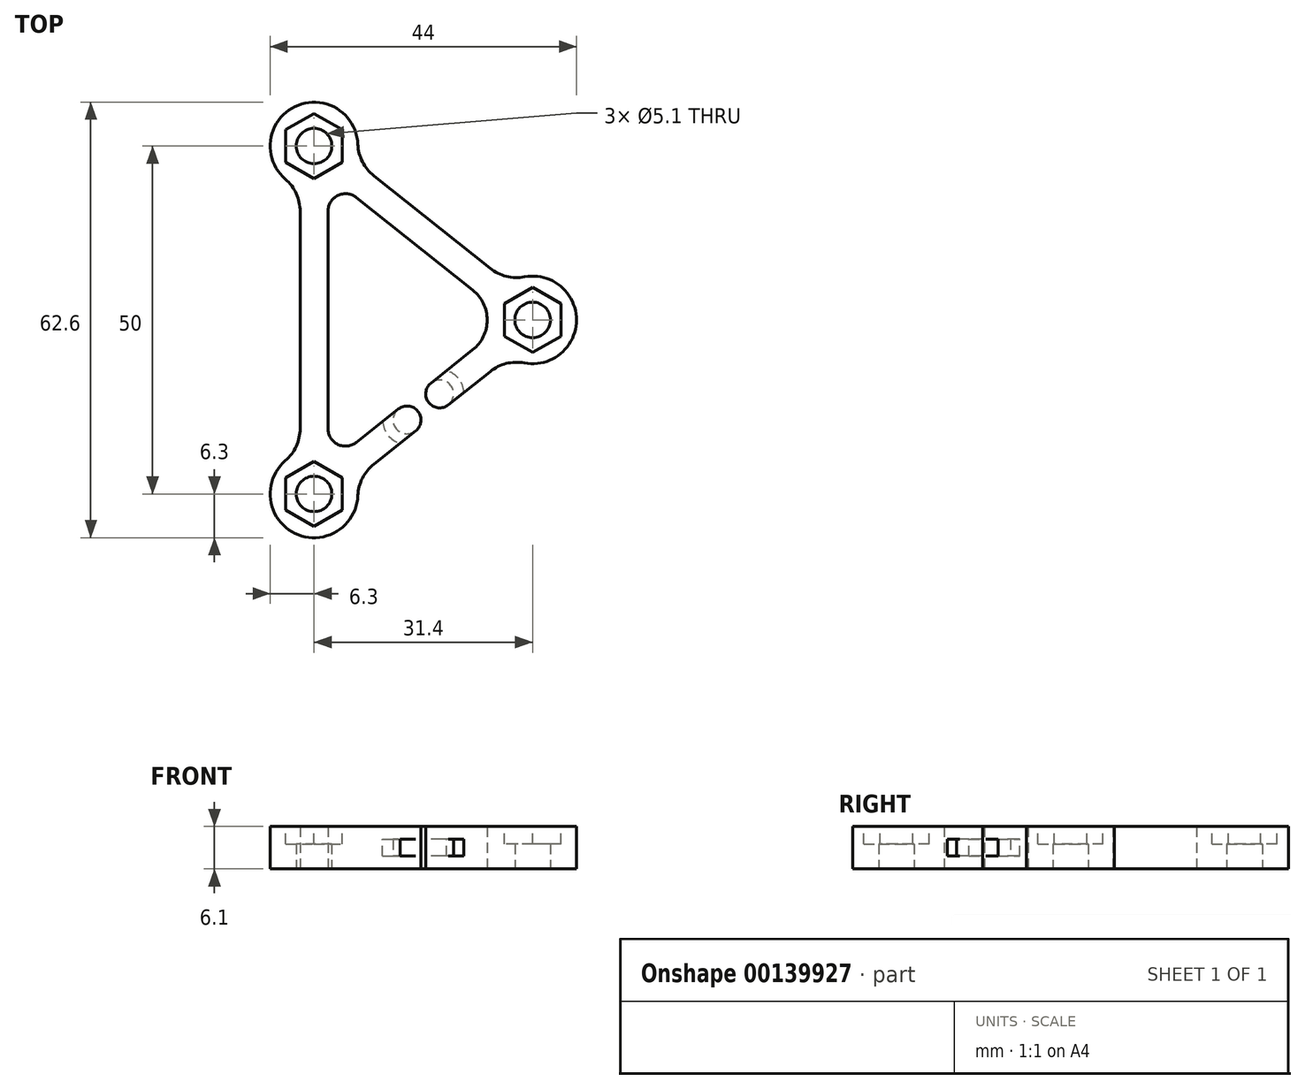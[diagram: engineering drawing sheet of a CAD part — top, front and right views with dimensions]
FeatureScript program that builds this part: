
annotation { "Feature Type Name" : "Feature", "Feature Type Description" : "" }
export const myFeature = defineFeature(function(context is Context, id is Id, definition is map)
    precondition{}
    {
        {
            var Q0;
            Q0=qCreatedBy(makeId("Top.planeOp"),FACE);
            var sketch = newSketch(context, id + "F0", { "sketchPlane" : qUnion([Q0])});
            skCircle(sketch, "E0", {"center": v(-31.4, 25) * mm, "radius": 2.55 * mm});
            skCircle(sketch, "E1", {"center": v(-31.4, -25) * mm, "radius": 2.55 * mm});
            skCircle(sketch, "E2", {"center": v(0, 0) * mm, "radius": 2.55 * mm});
            skArc(sketch, "E3", {"start": v(-25.1, 25.25) * mm, "mid": v(-34.14, 30.68) * mm, "end": v(-35.52, 20.23) * mm});
            skArc(sketch, "E4", {"start": v(-35.52, -20.23) * mm, "mid": v(-34.14, -30.68) * mm, "end": v(-25.1, -25.25) * mm});
            skArc(sketch, "E5", {"start": v(-1.17, -6.2) * mm, "mid": v(6.3, 0) * mm, "end": v(-1.17, 6.2) * mm});
            skLineSegment(sketch, "E6", {"start": v(-25.3, 17.59) * mm, "end": v(-8.6, 4.28) * mm});
            skLineSegment(sketch, "E7", {"start": v(-22.8, 20.72) * mm, "end": v(-6.1, 7.41) * mm});
            skLineSegment(sketch, "E8", {"start": v(-31.4, 25) * mm, "end": v(0, 0) * mm, "construction": true});
            skLineSegment(sketch, "E9", {"start": v(0, 0) * mm, "end": v(-31.4, -25) * mm, "construction": true});
            skLineSegment(sketch, "E10", {"start": v(-31.4, -25) * mm, "end": v(-31.4, 25) * mm, "construction": true});
            skArc(sketch, "E11", {"start": v(-25.3, 17.59) * mm, "mid": v(-27.97, 17.89) * mm, "end": v(-29.4, 15.61) * mm});
            skArc(sketch, "E12", {"start": v(-29.4, -15.61) * mm, "mid": v(-27.97, -17.89) * mm, "end": v(-25.3, -17.59) * mm});
            skArc(sketch, "E13", {"start": v(-8.6, -4.28) * mm, "mid": v(-6.53, 0) * mm, "end": v(-8.6, 4.28) * mm});
            skArc(sketch, "E14", {"start": v(-35.52, -20.23) * mm, "mid": v(-33.95, -18.15) * mm, "end": v(-33.4, -15.61) * mm});
            skArc(sketch, "E15", {"start": v(-22.8, -20.72) * mm, "mid": v(-24.45, -22.73) * mm, "end": v(-25.1, -25.25) * mm});
            skArc(sketch, "E16", {"start": v(-33.4, 15.61) * mm, "mid": v(-33.95, 18.15) * mm, "end": v(-35.52, 20.23) * mm});
            skArc(sketch, "E17", {"start": v(-25.1, 25.25) * mm, "mid": v(-24.45, 22.73) * mm, "end": v(-22.8, 20.72) * mm});
            skArc(sketch, "E18", {"start": v(-6.1, 7.41) * mm, "mid": v(-3.77, 6.26) * mm, "end": v(-1.17, 6.2) * mm});
            skArc(sketch, "E19", {"start": v(-1.17, -6.2) * mm, "mid": v(-3.77, -6.26) * mm, "end": v(-6.1, -7.41) * mm});
            skLineSegment(sketch, "E20", {"start": v(-25.3, 17.59) * mm, "end": v(-22.8, 20.72) * mm, "construction": true});
            skLineSegment(sketch, "E21", {"start": v(-8.6, 4.28) * mm, "end": v(-6.1, 7.41) * mm, "construction": true});
            skLineSegment(sketch, "E22", {"start": v(-8.6, -4.28) * mm, "end": v(-6.1, -7.41) * mm, "construction": true});
            skLineSegment(sketch, "E23", {"start": v(-33.4, -15.61) * mm, "end": v(-29.4, -15.61) * mm, "construction": true});
            skLineSegment(sketch, "E24", {"start": v(-22.8, -20.72) * mm, "end": v(-25.3, -17.59) * mm, "construction": true});
            skLineSegment(sketch, "E25", {"start": v(-33.4, -15.61) * mm, "end": v(-33.4, 15.61) * mm});
            skLineSegment(sketch, "E26", {"start": v(-29.4, -15.61) * mm, "end": v(-29.4, 15.61) * mm});
            skLineSegment(sketch, "E27", {"start": v(-33.4, 15.61) * mm, "end": v(-29.4, 15.61) * mm, "construction": true});
            skLineSegment(sketch, "E28", {"start": v(-25.3, -17.59) * mm, "end": v(-19.3, -12.8) * mm});
            skLineSegment(sketch, "E29", {"start": v(-14.6, -9.07) * mm, "end": v(-8.6, -4.28) * mm});
            skLineSegment(sketch, "E30", {"start": v(-22.8, -20.72) * mm, "end": v(-16.8, -15.93) * mm});
            skLineSegment(sketch, "E31", {"start": v(-6.1, -7.41) * mm, "end": v(-12.1, -12.2) * mm});
            skArc(sketch, "E32", {"start": v(-16.8, -15.93) * mm, "mid": v(-16.48, -13.12) * mm, "end": v(-19.3, -12.8) * mm});
            skArc(sketch, "E33", {"start": v(-14.6, -9.07) * mm, "mid": v(-14.92, -11.88) * mm, "end": v(-12.1, -12.2) * mm});
            skLineSegment(sketch, "E34", {"start": v(-29.4, 0) * mm, "end": v(0, 0) * mm, "construction": true});
            skSolve(sketch);
        }
        {
            var Q0;
            Q0=makeQuery(id+"F0.imprint","IMPRINT",FACE,{"disambiguationData":[TD([[makeQuery(id+"F0.imprint","IMPRINT",EDGE,{"derivedFrom":sQuery(id+"F0.wireOp",EDGE,"E0")}),-1.0]])]});
            extrude(context, id + "F1", {"entities" : qUnion([Q0]), "depth" : 6.1 * mm});
        }
        {
            var Q0;
            Q0=makeQuery(id+"F1.opExtrude","CAP_FACE",FACE,{"disambiguationData":[OSD([sQuery(id+"F0.wireOp",EDGE,"E0"),sQuery(id+"F0.wireOp",EDGE,"E1"),sQuery(id+"F0.wireOp",EDGE,"E2"),sQuery(id+"F0.wireOp",EDGE,"E3"),sQuery(id+"F0.wireOp",EDGE,"E4"),sQuery(id+"F0.wireOp",EDGE,"E5"),sQuery(id+"F0.wireOp",EDGE,"T5Vw66OG-G5OR-DHDx-KvU7-dnTMRq0o1A0g"),sQuery(id+"F0.wireOp",EDGE,"8mzCXc7P-Lu7A-tcA2-hDls-zUZMRrlwUirj"),sQuery(id+"F0.wireOp",EDGE,"n4Ubmgs8-MzYA-ilAs-um63-DOsCIZ42xYd5"),sQuery(id+"F0.wireOp",EDGE,"iCspHw3C-Pdpp-QPBW-yDHl-MGOv44Ga2VXa"),sQuery(id+"F0.wireOp",EDGE,"xnWTmErK-ZSIG-ryMW-Ekzr-RR3PqCajZfuL"),sQuery(id+"F0.wireOp",EDGE,"AKW5OVUo-PFRE-jSi0-v7oE-Iw4JobIG5vWv"),sQuery(id+"F0.wireOp",EDGE,"E6"),sQuery(id+"F0.wireOp",EDGE,"JkiSf5jC-OJZR-1wmq-AVkU-QwjWYPwXVpW3"),sQuery(id+"F0.wireOp",EDGE,"9YlTFYq7-sXvY-dmJ4-6YRE-gBgDyT6P94yA")])],"isStart":false});
            var sketch = newSketch(context, id + "F2", { "sketchPlane" : qUnion([Q0])});
            skCircle(sketch, "E35.cCircle", {"center": v(-31.4, 25) * mm, "radius": 4.05 * mm, "construction": true});
            skLineSegment(sketch, "E35.0", {"start": v(-27.35, 27.34) * mm, "end": v(-27.35, 22.66) * mm});
            skLineSegment(sketch, "E35.1", {"start": v(-27.35, 22.66) * mm, "end": v(-31.4, 20.32) * mm});
            skLineSegment(sketch, "E35.2", {"start": v(-31.4, 20.32) * mm, "end": v(-35.45, 22.66) * mm});
            skLineSegment(sketch, "E35.3", {"start": v(-35.45, 22.66) * mm, "end": v(-35.45, 27.34) * mm});
            skLineSegment(sketch, "E35.4", {"start": v(-35.45, 27.34) * mm, "end": v(-31.4, 29.68) * mm});
            skLineSegment(sketch, "E35.5", {"start": v(-31.4, 29.68) * mm, "end": v(-27.35, 27.34) * mm});
            skPoint(sketch, "E35.0.midPoint", {"position": v(-27.35, 25) * mm});
            skCircle(sketch, "E36.cCircle", {"center": v(-31.4, -25) * mm, "radius": 4.05 * mm, "construction": true});
            skLineSegment(sketch, "E36.0", {"start": v(-27.35, -22.66) * mm, "end": v(-27.35, -27.34) * mm});
            skLineSegment(sketch, "E36.1", {"start": v(-27.35, -27.34) * mm, "end": v(-31.4, -29.68) * mm});
            skLineSegment(sketch, "E36.2", {"start": v(-31.4, -29.68) * mm, "end": v(-35.45, -27.34) * mm});
            skLineSegment(sketch, "E36.3", {"start": v(-35.45, -27.34) * mm, "end": v(-35.45, -22.66) * mm});
            skLineSegment(sketch, "E36.4", {"start": v(-35.45, -22.66) * mm, "end": v(-31.4, -20.32) * mm});
            skLineSegment(sketch, "E36.5", {"start": v(-31.4, -20.32) * mm, "end": v(-27.35, -22.66) * mm});
            skPoint(sketch, "E36.0.midPoint", {"position": v(-27.35, -25) * mm});
            skCircle(sketch, "E37.cCircle", {"center": v(0, 0) * mm, "radius": 4.05 * mm, "construction": true});
            skLineSegment(sketch, "E37.0", {"start": v(-4.05, -2.34) * mm, "end": v(-4.05, 2.34) * mm});
            skLineSegment(sketch, "E37.1", {"start": v(-4.05, 2.34) * mm, "end": v(0, 4.68) * mm});
            skLineSegment(sketch, "E37.2", {"start": v(0, 4.68) * mm, "end": v(4.05, 2.34) * mm});
            skLineSegment(sketch, "E37.3", {"start": v(4.05, 2.34) * mm, "end": v(4.05, -2.34) * mm});
            skLineSegment(sketch, "E37.4", {"start": v(4.05, -2.34) * mm, "end": v(0, -4.68) * mm});
            skLineSegment(sketch, "E37.5", {"start": v(0, -4.68) * mm, "end": v(-4.05, -2.34) * mm});
            skPoint(sketch, "E37.0.midPoint", {"position": v(-4.05, 0) * mm});
            skSolve(sketch);
        }
        {
            var Q0;
            Q0=qSketchRegion(id+"F2",true);
            extrude(context, id + "F3", {"entities" : qUnion([Q0]), "operationType" : NewBodyOperationType.REMOVE, "oppositeDirection" : true, "depth" : 2.5 * mm});
        }
        {
            var Q0;
            Q0=qCreatedBy(makeId("Top.planeOp"),FACE);
            var Q1;
            Q1=makeQuery(id+"F2.imprint","IMPRINT",FACE,{"disambiguationData":[TD([[makeQuery(id+"F2.imprint","IMPRINT",EDGE,{"derivedFrom":sQuery(id+"F2.wireOp",EDGE,"E35.0")}),1.0]])]});
            cPlane(context, id + "F4", {"entities" : qUnion([Q0, Q1]), "cplaneType" : CPlaneType.MID_PLANE, "offset" : 3 * mm, "oppositeDirection" : true, "width" : 150 * mm, "height" : 150 * mm});
        }
        {
            var Q0;
            Q0=qCreatedBy(id+"F4.planeOp",FACE);
            var sketch = newSketch(context, id + "F5", { "sketchPlane" : qUnion([Q0])});
            skLineSegment(sketch, "E38", {"start": v(-16.8, -15.93) * mm, "end": v(-16.8, -15.93) * mm});
            skLineSegment(sketch, "E39", {"start": v(-19.3, -12.8) * mm, "end": v(-19.3, -12.8) * mm});
            skLineSegment(sketch, "E40", {"start": v(-12.1, -12.2) * mm, "end": v(-12.1, -12.2) * mm});
            skLineSegment(sketch, "E41", {"start": v(-14.6, -9.07) * mm, "end": v(-14.6, -9.07) * mm});
            skArc(sketch, "E42", {"start": v(-21.54, -14.6) * mm, "mid": v(-20.79, -16.55) * mm, "end": v(-19.05, -17.72) * mm});
            skArc(sketch, "E43", {"start": v(-12.1, -12.2) * mm, "mid": v(-11.79, -9.39) * mm, "end": v(-14.6, -9.07) * mm});
            skArc(sketch, "E44", {"start": v(-19.3, -12.8) * mm, "mid": v(-19.61, -15.61) * mm, "end": v(-16.8, -15.93) * mm});
            skLineSegment(sketch, "E45", {"start": v(-21.54, -14.6) * mm, "end": v(-19.3, -12.8) * mm});
            skLineSegment(sketch, "E46", {"start": v(-16.8, -15.93) * mm, "end": v(-19.05, -17.72) * mm});
            skArc(sketch, "E47", {"start": v(-9.86, -10.4) * mm, "mid": v(-10.61, -8.45) * mm, "end": v(-12.35, -7.28) * mm});
            skLineSegment(sketch, "E48", {"start": v(-12.35, -7.28) * mm, "end": v(-14.6, -9.07) * mm});
            skLineSegment(sketch, "E49", {"start": v(-12.1, -12.2) * mm, "end": v(-9.86, -10.4) * mm});
            skSolve(sketch);
        }
        {
            var Q0;
            Q0=qSketchRegion(id+"F5",true);
            extrude(context, id + "F6", {"entities" : qUnion([Q0]), "operationType" : NewBodyOperationType.REMOVE, "oppositeDirection" : true, "depth" : 2.4 * mm, "symmetric" : true});
        }
    });
